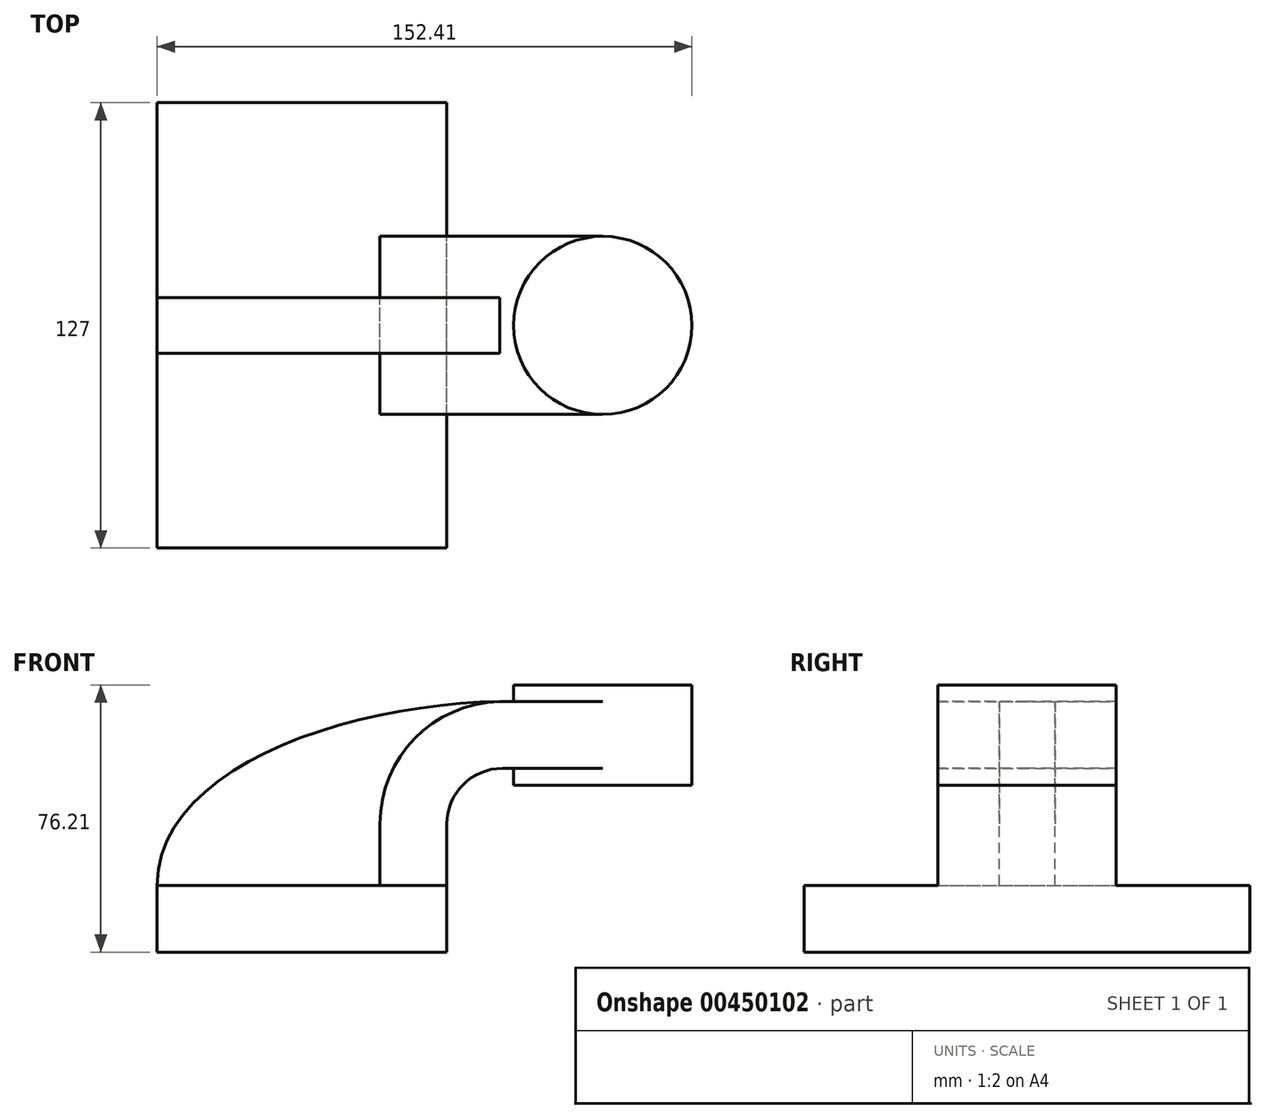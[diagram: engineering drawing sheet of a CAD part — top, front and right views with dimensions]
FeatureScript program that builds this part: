
annotation { "Feature Type Name" : "Feature", "Feature Type Description" : "" }
export const myFeature = defineFeature(function(context is Context, id is Id, definition is map)
    precondition{}
    {
        {
            var Q0;
            Q0=qCreatedBy(makeId("Front.planeOp"),FACE);
            var sketch = newSketch(context, id + "F0", { "sketchPlane" : qUnion([Q0])});
            skLineSegment(sketch, "E0.bottom", {"start": v(-41.28, -9.53) * mm, "end": v(41.28, -9.53) * mm});
            skLineSegment(sketch, "E0.top", {"start": v(-41.28, 9.53) * mm, "end": v(41.28, 9.53) * mm});
            skLineSegment(sketch, "E0.left", {"start": v(-41.28, -9.53) * mm, "end": v(-41.28, 9.53) * mm});
            skLineSegment(sketch, "E0.right", {"start": v(41.28, -9.53) * mm, "end": v(41.28, 9.53) * mm});
            skPoint(sketch, "E0.middle", {"position": v(0, 0) * mm});
            skLineSegment(sketch, "E1.bottom", {"start": v(60.32, 38.1) * mm, "end": v(111.12, 38.1) * mm});
            skLineSegment(sketch, "E1.top", {"start": v(60.32, 66.67) * mm, "end": v(111.12, 66.67) * mm});
            skLineSegment(sketch, "E1.left", {"start": v(60.32, 38.1) * mm, "end": v(60.32, 66.68) * mm});
            skLineSegment(sketch, "E1.right", {"start": v(111.12, 38.1) * mm, "end": v(111.12, 66.68) * mm});
            skPoint(sketch, "E1.middle", {"position": v(85.72, 52.39) * mm});
            skLineSegment(sketch, "E2", {"start": v(41.27, 9.52) * mm, "end": v(41.27, 27) * mm});
            skArc(sketch, "E3", {"start": v(41.27, 27) * mm, "mid": v(45.92, 38.23) * mm, "end": v(57.15, 42.88) * mm});
            skLineSegment(sketch, "E4", {"start": v(57.15, 42.88) * mm, "end": v(85.72, 42.88) * mm});
            skLineSegment(sketch, "E5.0", {"start": v(57.15, 61.93) * mm, "end": v(85.72, 61.93) * mm});
            skArc(sketch, "E5.1", {"start": v(22.23, 27) * mm, "mid": v(32.45, 51.7) * mm, "end": v(57.15, 61.93) * mm});
            skLineSegment(sketch, "E5.2", {"start": v(22.22, 9.52) * mm, "end": v(22.22, 27) * mm});
            skLineSegment(sketch, "E6", {"start": v(85.72, 38.1) * mm, "end": v(85.72, 66.67) * mm});
            skFitSpline(sketch, "E7", {"points": [v(-41.28, 9.53) * mm, v(57.15, 61.93) * mm], "startDerivative": vector(0.78, 103.83) * mm, "endDerivative": vector(125.98, 1.2) * mm});
            skSolve(sketch);
        }
        {
            var Q0;
            Q0=makeQuery(id+"F0.imprint","IMPRINT",FACE,{"disambiguationData":[TD([[makeQuery(id+"F0.imprint","IMPRINT",EDGE,{"derivedFrom":sQuery(id+"F0.wireOp",EDGE,"E0.bottom")}),1.0]])]});
            extrude(context, id + "F1", {"entities" : qUnion([Q0]), "endBound" : BoundingType.SYMMETRIC, "depth" : 127 * mm});
        }
        {
            var Q0;
            {var subQ0=sQuery(id+"F0.wireOp",EDGE,"E4");var subQ1=sQuery(id+"F0.wireOp",EDGE,"E1.left");var subQ2=makeQuery(id+"F0.imprint","INTERSECT",VERTEX,{"derivedFrom":[subQ1,subQ0]});Q0=makeQuery(id+"F0.imprint","IMPRINT",FACE,{"disambiguationData":[TD([[makeQuery(id+"F0.imprint","IMPRINT",EDGE,{"disambiguationData":[TD([[subQ2,-1.0]])],"derivedFrom":subQ1}),-1.0]])]});}
            var Q1;
            {var subQ1=sQuery(id+"F0.wireOp",EDGE,"E2");Q1=makeQuery(id+"F0.imprint","IMPRINT",FACE,{"disambiguationData":[TD([[makeQuery(id+"F0.imprint","IMPRINT",EDGE,{"derivedFrom":subQ1}),1.0]])]});}
            extrude(context, id + "F2", {"entities" : qUnion([Q0, Q1]), "operationType" : NewBodyOperationType.ADD, "endBound" : BoundingType.SYMMETRIC, "depth" : 50.8 * mm});
        }
        {
            var Q0;
            {var subQ3=sQuery(id+"F0.wireOp",EDGE,"E5.2");Q0=makeQuery(id+"F0.imprint","IMPRINT",FACE,{"disambiguationData":[TD([[makeQuery(id+"F0.imprint","IMPRINT",EDGE,{"derivedFrom":subQ3}),1.0]])]});}
            extrude(context, id + "F3", {"entities" : qUnion([Q0]), "endBound" : BoundingType.SYMMETRIC, "depth" : 15.88 * mm});
        }
        {
            var Q0;
            {var subQ4=sQuery(id+"F0.wireOp",EDGE,"E1.right");Q0=makeQuery(id+"F0.imprint","IMPRINT",FACE,{"disambiguationData":[TD([[makeQuery(id+"F0.imprint","IMPRINT",EDGE,{"derivedFrom":subQ4}),1.0]])]});}
            var Q1;
            Q1=sQuery(id+"F0.wireOp",EDGE,"E6");
            revolve(context, id + "F4", {"operationType" : NewBodyOperationType.ADD, "entities" : qUnion([Q0]), "axis" : qUnion([Q1]), "revolveType" : RevolveType.FULL});
        }
    });
